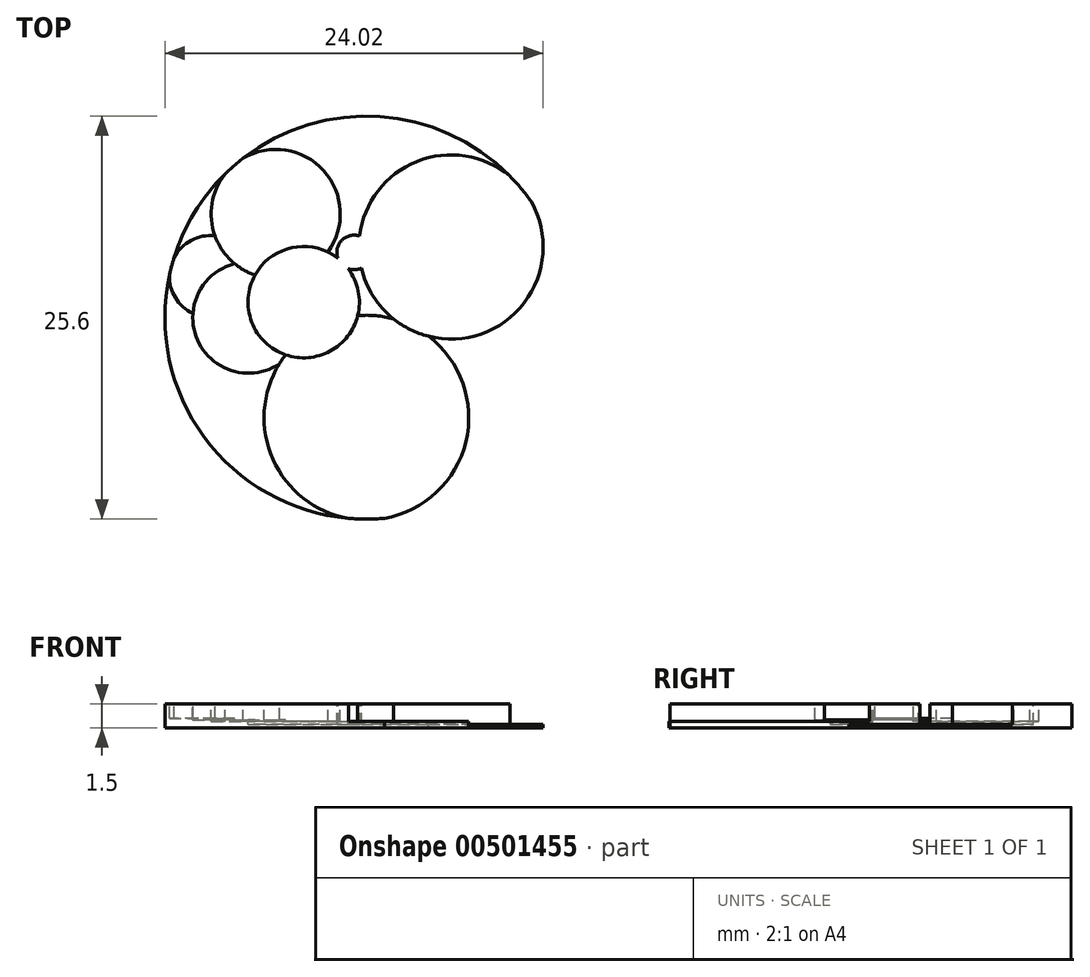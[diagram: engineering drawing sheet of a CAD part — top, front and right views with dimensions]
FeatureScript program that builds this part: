
annotation { "Feature Type Name" : "Feature", "Feature Type Description" : "" }
export const myFeature = defineFeature(function(context is Context, id is Id, definition is map)
    precondition{}
    {
        {
            var Q0;
            Q0=qCreatedBy(makeId("Top.planeOp"),FACE);
            var sketch = newSketch(context, id + "F0", { "sketchPlane" : qUnion([Q0])});
            skCircle(sketch, "E0", {"center": v(0, 0) * mm, "radius": 12.8 * mm});
            skCircle(sketch, "E1", {"center": v(5.37, 4.5) * mm, "radius": 5.65 * mm, "construction": true});
            skCircle(sketch, "E2", {"center": v(-0.78, 4.14) * mm, "radius": 4.05 * mm, "construction": true});
            skCircle(sketch, "E3", {"center": v(-0.78, 4.14) * mm, "radius": 0.9 * mm, "construction": true});
            skCircle(sketch, "E4", {"center": v(-3.98, 0.99) * mm, "radius": 3.34 * mm, "construction": true});
            skCircle(sketch, "E5", {"center": v(-3.98, 0.99) * mm, "radius": 0.63 * mm, "construction": true});
            skCircle(sketch, "E6", {"center": v(-7.5, 0) * mm, "radius": 3.33 * mm, "construction": true});
            skCircle(sketch, "E7", {"center": v(-7.5, 0) * mm, "radius": 0.47 * mm, "construction": true});
            skLineSegment(sketch, "E8", {"start": v(0, 12.8) * mm, "end": v(0, 5.1) * mm, "construction": true});
            skCircle(sketch, "E9", {"center": v(5.37, 4.5) * mm, "radius": 5.15 * mm, "construction": true});
            skCircle(sketch, "E10", {"center": v(0, -6.35) * mm, "radius": 6.3 * mm, "construction": true});
            skCircle(sketch, "E11", {"center": v(-9.91, 2.61) * mm, "radius": 0.38 * mm, "construction": true});
            skCircle(sketch, "E12", {"center": v(-9.91, 2.61) * mm, "radius": 2.4 * mm, "construction": true});
            skCircle(sketch, "E13", {"center": v(-5.76, 6.59) * mm, "radius": 3.85 * mm, "construction": true});
            skLineSegment(sketch, "E14", {"start": v(12.8, 0) * mm, "end": v(5.1, 0) * mm, "construction": true});
            skCircle(sketch, "E15", {"center": v(0, 5.4) * mm, "radius": 0.3 * mm, "construction": true});
            skCircle(sketch, "E16", {"center": v(5.37, 4.5) * mm, "radius": 6.16 * mm, "construction": true});
            skCircle(sketch, "E17", {"center": v(-0.78, 4.14) * mm, "radius": 4.5 * mm, "construction": true});
            skCircle(sketch, "E18", {"center": v(-3.98, 0.99) * mm, "radius": 3.65 * mm, "construction": true});
            skCircle(sketch, "E19", {"center": v(-7.5, 0) * mm, "radius": 3.56 * mm, "construction": true});
            skLineSegment(sketch, "E20", {"start": v(-9.91, 2.61) * mm, "end": v(-5.76, 6.59) * mm, "construction": true});
            skCircle(sketch, "E21", {"center": v(0, 6.2) * mm, "radius": 1.26 * mm, "construction": true});
            skCircle(sketch, "E22", {"center": v(0, 0) * mm, "radius": 1.16 * mm, "construction": true});
            skCircle(sketch, "E23", {"center": v(-0.78, 4.14) * mm, "radius": 1.16 * mm, "construction": true});
            skCircle(sketch, "E24", {"center": v(0, 6.2) * mm, "radius": 2.2 * mm, "construction": true});
            skCircle(sketch, "E25", {"center": v(0, 0) * mm, "radius": 2.81 * mm, "construction": true});
            skCircle(sketch, "E26", {"center": v(-5.76, 6.59) * mm, "radius": 2 * mm, "construction": true});
            skArc(sketch, "E27", {"start": v(1.14, -12.75) * mm, "mid": v(0, 0.15) * mm, "end": v(-1.14, -12.75) * mm});
            skCircle(sketch, "E28", {"center": v(-7.5, 0) * mm, "radius": 3.53 * mm});
            skArc(sketch, "E29", {"start": v(-12.5, 2.71) * mm, "mid": v(-7.4, 1.95) * mm, "end": v(-12.22, 3.8) * mm});
            skArc(sketch, "E30", {"start": v(9.1, 9) * mm, "mid": v(0.89, 0.74) * mm, "end": v(10.47, 7.36) * mm});
            skCircle(sketch, "E31", {"center": v(-3.98, 0.99) * mm, "radius": 3.54 * mm});
            skCircle(sketch, "E32", {"center": v(-0.78, 4.14) * mm, "radius": 1.1 * mm});
            skCircle(sketch, "E33", {"center": v(-5.76, 6.59) * mm, "radius": 4.1 * mm});
            skArc(sketch, "E34", {"start": v(-1.14, -12.75) * mm, "mid": v(0, -12.85) * mm, "end": v(1.14, -12.75) * mm});
            skArc(sketch, "E35", {"start": v(10.47, 7.36) * mm, "mid": v(9.86, 8.24) * mm, "end": v(9.1, 9) * mm});
            skArc(sketch, "E36", {"start": v(-12.22, 3.8) * mm, "mid": v(-12.43, 3.28) * mm, "end": v(-12.5, 2.71) * mm});
            skSolve(sketch);
        }
        {
            var Q0;
            {var subQ0=sQuery(id+"F0.wireOp",EDGE,"E31");var subQ1=sQuery(id+"F0.wireOp",EDGE,"E28");var subQ2=makeQuery(id+"F0.imprint","INTERSECT",VERTEX,{"disambiguationData":[OD(0.0)],"derivedFrom":[subQ1,subQ0]});Q0=makeQuery(id+"F0.imprint","IMPRINT",FACE,{"disambiguationData":[TD([[makeQuery(id+"F0.imprint","IMPRINT",EDGE,{"disambiguationData":[TD([[subQ2,1.0]])],"derivedFrom":subQ1}),1.0]])]});}
            var Q1;
            {var subQ0=sQuery(id+"F0.wireOp",EDGE,"E29");var subQ1=sQuery(id+"F0.wireOp",EDGE,"E0");var subQ2=makeQuery(id+"F0.imprint","INTERSECT",VERTEX,{"disambiguationData":[OD(1.0)],"derivedFrom":[subQ1,subQ0]});Q1=makeQuery(id+"F0.imprint","IMPRINT",FACE,{"disambiguationData":[TD([[makeQuery(id+"F0.imprint","IMPRINT",EDGE,{"disambiguationData":[TD([[subQ2,1.0]])],"derivedFrom":subQ1}),1.0]])]});}
            var Q2;
            {var subQ0=sQuery(id+"F0.wireOp",EDGE,"E28");var subQ1=sQuery(id+"F0.wireOp",EDGE,"E27");var subQ2=makeQuery(id+"F0.imprint","INTERSECT",VERTEX,{"disambiguationData":[OD(0.0)],"derivedFrom":[subQ1,subQ0]});Q2=makeQuery(id+"F0.imprint","IMPRINT",FACE,{"disambiguationData":[TD([[makeQuery(id+"F0.imprint","IMPRINT",EDGE,{"disambiguationData":[TD([[subQ2,-1.0]])],"derivedFrom":subQ1}),1.0]])]});}
            var Q3;
            {var subQ0=sQuery(id+"F0.wireOp",EDGE,"E31");var subQ1=sQuery(id+"F0.wireOp",EDGE,"E27");var subQ2=makeQuery(id+"F0.imprint","INTERSECT",VERTEX,{"disambiguationData":[OD(1.0)],"derivedFrom":[subQ1,subQ0]});Q3=makeQuery(id+"F0.imprint","IMPRINT",FACE,{"disambiguationData":[TD([[makeQuery(id+"F0.imprint","IMPRINT",EDGE,{"disambiguationData":[TD([[subQ2,-1.0]])],"derivedFrom":subQ1}),-1.0]])]});}
            var Q4;
            {var subQ0=sQuery(id+"F0.wireOp",EDGE,"E33");var subQ1=sQuery(id+"F0.wireOp",EDGE,"E28");var subQ2=makeQuery(id+"F0.imprint","INTERSECT",VERTEX,{"disambiguationData":[OD(1.0)],"derivedFrom":[subQ1,subQ0]});Q4=makeQuery(id+"F0.imprint","IMPRINT",FACE,{"disambiguationData":[TD([[makeQuery(id+"F0.imprint","IMPRINT",EDGE,{"disambiguationData":[TD([[subQ2,-1.0]])],"derivedFrom":subQ1}),1.0]])]});}
            var Q5;
            {var subQ0=sQuery(id+"F0.wireOp",EDGE,"E29");var subQ1=sQuery(id+"F0.wireOp",EDGE,"E0");var subQ5=makeQuery(id+"F0.imprint","INTERSECT",VERTEX,{"disambiguationData":[OD(0.0)],"derivedFrom":[subQ1,subQ0]});Q5=makeQuery(id+"F0.imprint","IMPRINT",FACE,{"disambiguationData":[TD([[makeQuery(id+"F0.imprint","IMPRINT",EDGE,{"disambiguationData":[TD([[subQ5,1.0]])],"derivedFrom":subQ1}),1.0]])]});}
            var Q6;
            {var subQ0=sQuery(id+"F0.wireOp",EDGE,"E32");var subQ1=sQuery(id+"F0.wireOp",EDGE,"E30");var subQ2=makeQuery(id+"F0.imprint","INTERSECT",VERTEX,{"disambiguationData":[OD(0.0)],"derivedFrom":[subQ1,subQ0]});Q6=makeQuery(id+"F0.imprint","IMPRINT",FACE,{"disambiguationData":[TD([[makeQuery(id+"F0.imprint","IMPRINT",EDGE,{"disambiguationData":[TD([[subQ2,-1.0]])],"derivedFrom":subQ1}),1.0]])]});}
            var Q7;
            {var subQ0=sQuery(id+"F0.wireOp",EDGE,"E29");var subQ1=sQuery(id+"F0.wireOp",EDGE,"E28");var subQ2=makeQuery(id+"F0.imprint","INTERSECT",VERTEX,{"disambiguationData":[OD(0.0)],"derivedFrom":[subQ1,subQ0]});Q7=makeQuery(id+"F0.imprint","IMPRINT",FACE,{"disambiguationData":[TD([[makeQuery(id+"F0.imprint","IMPRINT",EDGE,{"disambiguationData":[TD([[subQ2,-1.0]])],"derivedFrom":subQ1}),1.0]])]});}
            var Q8;
            {var subQ0=sQuery(id+"F0.wireOp",EDGE,"E29");var subQ1=sQuery(id+"F0.wireOp",EDGE,"E28");var subQ2=makeQuery(id+"F0.imprint","INTERSECT",VERTEX,{"disambiguationData":[OD(0.0)],"derivedFrom":[subQ1,subQ0]});Q8=makeQuery(id+"F0.imprint","IMPRINT",FACE,{"disambiguationData":[TD([[makeQuery(id+"F0.imprint","IMPRINT",EDGE,{"disambiguationData":[TD([[subQ2,-1.0]])],"derivedFrom":subQ1}),-1.0]])]});}
            var Q9;
            {var subQ4=sQuery(id+"F0.wireOp",EDGE,"E31");var subQ5=sQuery(id+"F0.wireOp",EDGE,"E28");var subQ6=makeQuery(id+"F0.imprint","INTERSECT",VERTEX,{"disambiguationData":[OD(0.0)],"derivedFrom":[subQ5,subQ4]});Q9=makeQuery(id+"F0.imprint","IMPRINT",FACE,{"disambiguationData":[TD([[makeQuery(id+"F0.imprint","IMPRINT",EDGE,{"disambiguationData":[TD([[subQ6,-1.0]])],"derivedFrom":subQ5}),-1.0]])]});}
            var Q10;
            {var subQ0=sQuery(id+"F0.wireOp",EDGE,"E31");var subQ1=sQuery(id+"F0.wireOp",EDGE,"E28");var subQ2=makeQuery(id+"F0.imprint","INTERSECT",VERTEX,{"disambiguationData":[OD(0.0)],"derivedFrom":[subQ1,subQ0]});Q10=makeQuery(id+"F0.imprint","IMPRINT",FACE,{"disambiguationData":[TD([[makeQuery(id+"F0.imprint","IMPRINT",EDGE,{"disambiguationData":[TD([[subQ2,-1.0]])],"derivedFrom":subQ1}),1.0]])]});}
            var Q11;
            {var subQ0=sQuery(id+"F0.wireOp",EDGE,"E31");var subQ1=sQuery(id+"F0.wireOp",EDGE,"E27");var subQ2=makeQuery(id+"F0.imprint","INTERSECT",VERTEX,{"disambiguationData":[OD(1.0)],"derivedFrom":[subQ1,subQ0]});Q11=makeQuery(id+"F0.imprint","IMPRINT",FACE,{"disambiguationData":[TD([[makeQuery(id+"F0.imprint","IMPRINT",EDGE,{"disambiguationData":[TD([[subQ2,-1.0]])],"derivedFrom":subQ1}),1.0]])]});}
            var Q12;
            {var subQ0=sQuery(id+"F0.wireOp",EDGE,"E31");var subQ1=sQuery(id+"F0.wireOp",EDGE,"E27");var subQ2=makeQuery(id+"F0.imprint","INTERSECT",VERTEX,{"disambiguationData":[OD(0.0)],"derivedFrom":[subQ1,subQ0]});Q12=makeQuery(id+"F0.imprint","IMPRINT",FACE,{"disambiguationData":[TD([[makeQuery(id+"F0.imprint","IMPRINT",EDGE,{"disambiguationData":[TD([[subQ2,-1.0]])],"derivedFrom":subQ1}),1.0]])]});}
            var Q13;
            {var subQ0=sQuery(id+"F0.wireOp",EDGE,"E31");var subQ1=sQuery(id+"F0.wireOp",EDGE,"E27");var subQ2=makeQuery(id+"F0.imprint","INTERSECT",VERTEX,{"disambiguationData":[OD(0.0)],"derivedFrom":[subQ1,subQ0]});Q13=makeQuery(id+"F0.imprint","IMPRINT",FACE,{"disambiguationData":[TD([[makeQuery(id+"F0.imprint","IMPRINT",EDGE,{"disambiguationData":[TD([[subQ2,-1.0]])],"derivedFrom":subQ1}),-1.0]])]});}
            var Q14;
            {var subQ0=sQuery(id+"F0.wireOp",EDGE,"E30");var subQ1=sQuery(id+"F0.wireOp",EDGE,"E27");var subQ2=makeQuery(id+"F0.imprint","INTERSECT",VERTEX,{"disambiguationData":[OD(0.0)],"derivedFrom":[subQ1,subQ0]});Q14=makeQuery(id+"F0.imprint","IMPRINT",FACE,{"disambiguationData":[TD([[makeQuery(id+"F0.imprint","IMPRINT",EDGE,{"disambiguationData":[TD([[subQ2,-1.0]])],"derivedFrom":subQ1}),1.0]])]});}
            var Q15;
            {var subQ0=sQuery(id+"F0.wireOp",EDGE,"E30");var subQ1=sQuery(id+"F0.wireOp",EDGE,"E27");var subQ2=makeQuery(id+"F0.imprint","INTERSECT",VERTEX,{"disambiguationData":[OD(1.0)],"derivedFrom":[subQ1,subQ0]});Q15=makeQuery(id+"F0.imprint","IMPRINT",FACE,{"disambiguationData":[TD([[makeQuery(id+"F0.imprint","IMPRINT",EDGE,{"disambiguationData":[TD([[subQ2,-1.0]])],"derivedFrom":subQ1}),-1.0]])]});}
            var Q16;
            {var subQ1=sQuery(id+"F0.wireOp",EDGE,"E30");var subQ7=sQuery(id+"F0.wireOp",EDGE,"E0");var subQ8=makeQuery(id+"F0.imprint","INTERSECT",VERTEX,{"disambiguationData":[OD(0.0)],"derivedFrom":[subQ7,subQ1]});Q16=makeQuery(id+"F0.imprint","IMPRINT",FACE,{"disambiguationData":[TD([[makeQuery(id+"F0.imprint","IMPRINT",EDGE,{"disambiguationData":[TD([[subQ8,-1.0]])],"derivedFrom":subQ7}),1.0]])]});}
            var Q17;
            {var subQ0=sQuery(id+"F0.wireOp",EDGE,"E31");var subQ1=sQuery(id+"F0.wireOp",EDGE,"E28");var subQ2=makeQuery(id+"F0.imprint","INTERSECT",VERTEX,{"disambiguationData":[OD(0.0)],"derivedFrom":[subQ1,subQ0]});Q17=makeQuery(id+"F0.imprint","IMPRINT",FACE,{"disambiguationData":[TD([[makeQuery(id+"F0.imprint","IMPRINT",EDGE,{"disambiguationData":[TD([[subQ2,1.0]])],"derivedFrom":subQ1}),-1.0]])]});}
            var Q18;
            {var subQ0=sQuery(id+"F0.wireOp",EDGE,"E28");var subQ1=sQuery(id+"F0.wireOp",EDGE,"E27");var subQ2=makeQuery(id+"F0.imprint","INTERSECT",VERTEX,{"disambiguationData":[OD(0.0)],"derivedFrom":[subQ1,subQ0]});Q18=makeQuery(id+"F0.imprint","IMPRINT",FACE,{"disambiguationData":[TD([[makeQuery(id+"F0.imprint","IMPRINT",EDGE,{"disambiguationData":[TD([[subQ2,-1.0]])],"derivedFrom":subQ1}),-1.0]])]});}
            var Q19;
            {var subQ0=sQuery(id+"F0.wireOp",EDGE,"E30");var subQ5=sQuery(id+"F0.wireOp",EDGE,"E0");var subQ6=makeQuery(id+"F0.imprint","INTERSECT",VERTEX,{"disambiguationData":[OD(0.0)],"derivedFrom":[subQ5,subQ0]});Q19=makeQuery(id+"F0.imprint","IMPRINT",FACE,{"disambiguationData":[TD([[makeQuery(id+"F0.imprint","IMPRINT",EDGE,{"disambiguationData":[TD([[subQ6,1.0]])],"derivedFrom":subQ5}),1.0]])]});}
            var Q20;
            {var subQ0=sQuery(id+"F0.wireOp",EDGE,"E32");var subQ1=sQuery(id+"F0.wireOp",EDGE,"E30");var subQ2=makeQuery(id+"F0.imprint","INTERSECT",VERTEX,{"disambiguationData":[OD(0.0)],"derivedFrom":[subQ1,subQ0]});Q20=makeQuery(id+"F0.imprint","IMPRINT",FACE,{"disambiguationData":[TD([[makeQuery(id+"F0.imprint","IMPRINT",EDGE,{"disambiguationData":[TD([[subQ2,-1.0]])],"derivedFrom":subQ1}),-1.0]])]});}
            var Q21;
            {var subQ0=sQuery(id+"F0.wireOp",EDGE,"E32");var subQ1=sQuery(id+"F0.wireOp",EDGE,"E31");var subQ2=makeQuery(id+"F0.imprint","INTERSECT",VERTEX,{"disambiguationData":[OD(0.0)],"derivedFrom":[subQ1,subQ0]});Q21=makeQuery(id+"F0.imprint","IMPRINT",FACE,{"disambiguationData":[TD([[makeQuery(id+"F0.imprint","IMPRINT",EDGE,{"disambiguationData":[TD([[subQ2,1.0]])],"derivedFrom":subQ1}),1.0]])]});}
            var Q22;
            {var subQ0=sQuery(id+"F0.wireOp",EDGE,"E27");var subQ1=sQuery(id+"F0.wireOp",EDGE,"E0");var subQ9=makeQuery(id+"F0.imprint","INTERSECT",VERTEX,{"disambiguationData":[OD(0.0)],"derivedFrom":[subQ1,subQ0]});Q22=makeQuery(id+"F0.imprint","IMPRINT",FACE,{"disambiguationData":[TD([[makeQuery(id+"F0.imprint","IMPRINT",EDGE,{"disambiguationData":[TD([[subQ9,1.0]])],"derivedFrom":subQ1}),1.0]])]});}
            var Q23;
            {var subQ0=sQuery(id+"F0.wireOp",EDGE,"E27");var subQ1=sQuery(id+"F0.wireOp",EDGE,"E0");var subQ2=makeQuery(id+"F0.imprint","INTERSECT",VERTEX,{"disambiguationData":[OD(1.0)],"derivedFrom":[subQ1,subQ0]});Q23=makeQuery(id+"F0.imprint","IMPRINT",FACE,{"disambiguationData":[TD([[makeQuery(id+"F0.imprint","IMPRINT",EDGE,{"disambiguationData":[TD([[subQ2,1.0]])],"derivedFrom":subQ1}),1.0]])]});}
            var Q24;
            {var subQ0=sQuery(id+"F0.wireOp",EDGE,"E27");var subQ1=sQuery(id+"F0.wireOp",EDGE,"E0");var subQ2=makeQuery(id+"F0.imprint","INTERSECT",VERTEX,{"disambiguationData":[OD(0.0)],"derivedFrom":[subQ1,subQ0]});Q24=makeQuery(id+"F0.imprint","IMPRINT",FACE,{"disambiguationData":[TD([[makeQuery(id+"F0.imprint","IMPRINT",EDGE,{"disambiguationData":[TD([[subQ2,-1.0]])],"derivedFrom":subQ1}),1.0]])]});}
            extrude(context, id + "F1", {"entities" : qUnion([Q0, Q1, Q2, Q3, Q4, Q5, Q6, Q7, Q8, Q9, Q10, Q11, Q12, Q13, Q14, Q15, Q16, Q17, Q18, Q19, Q20, Q21, Q22, Q23, Q24]), "oppositeDirection" : true, "depth" : 1.5 * mm, "offsetDistance" : 25 * mm});
        }
        {
            var Q0;
            {var subQ0=sQuery(id+"F0.wireOp",EDGE,"E34");Q0=makeQuery(id+"F0.imprint","IMPRINT",FACE,{"disambiguationData":[TD([[makeQuery(id+"F0.imprint","IMPRINT",EDGE,{"derivedFrom":subQ0}),1.0]])]});}
            var Q1;
            {var subQ1=sQuery(id+"F0.wireOp",EDGE,"E27");var subQ6=sQuery(id+"F0.wireOp",EDGE,"E30");var subQ7=makeQuery(id+"F0.imprint","INTERSECT",VERTEX,{"disambiguationData":[OD(1.0)],"derivedFrom":[subQ1,subQ6]});Q1=makeQuery(id+"F0.imprint","IMPRINT",FACE,{"disambiguationData":[TD([[makeQuery(id+"F0.imprint","IMPRINT",EDGE,{"disambiguationData":[TD([[subQ7,-1.0]])],"derivedFrom":subQ1}),1.0]])]});}
            var Q2;
            {var subQ0=sQuery(id+"F0.wireOp",EDGE,"E30");var subQ1=sQuery(id+"F0.wireOp",EDGE,"E27");var subQ2=makeQuery(id+"F0.imprint","INTERSECT",VERTEX,{"disambiguationData":[OD(0.0)],"derivedFrom":[subQ1,subQ0]});Q2=makeQuery(id+"F0.imprint","IMPRINT",FACE,{"disambiguationData":[TD([[makeQuery(id+"F0.imprint","IMPRINT",EDGE,{"disambiguationData":[TD([[subQ2,-1.0]])],"derivedFrom":subQ1}),1.0]])]});}
            var Q3;
            {var subQ0=sQuery(id+"F0.wireOp",EDGE,"E31");var subQ1=sQuery(id+"F0.wireOp",EDGE,"E27");var subQ2=makeQuery(id+"F0.imprint","INTERSECT",VERTEX,{"disambiguationData":[OD(0.0)],"derivedFrom":[subQ1,subQ0]});Q3=makeQuery(id+"F0.imprint","IMPRINT",FACE,{"disambiguationData":[TD([[makeQuery(id+"F0.imprint","IMPRINT",EDGE,{"disambiguationData":[TD([[subQ2,-1.0]])],"derivedFrom":subQ1}),1.0]])]});}
            var Q4;
            {var subQ0=sQuery(id+"F0.wireOp",EDGE,"E28");var subQ1=sQuery(id+"F0.wireOp",EDGE,"E27");var subQ2=makeQuery(id+"F0.imprint","INTERSECT",VERTEX,{"disambiguationData":[OD(0.0)],"derivedFrom":[subQ1,subQ0]});Q4=makeQuery(id+"F0.imprint","IMPRINT",FACE,{"disambiguationData":[TD([[makeQuery(id+"F0.imprint","IMPRINT",EDGE,{"disambiguationData":[TD([[subQ2,-1.0]])],"derivedFrom":subQ1}),1.0]])]});}
            var Q5;
            {var subQ0=sQuery(id+"F0.wireOp",EDGE,"E31");var subQ1=sQuery(id+"F0.wireOp",EDGE,"E27");var subQ2=makeQuery(id+"F0.imprint","INTERSECT",VERTEX,{"disambiguationData":[OD(1.0)],"derivedFrom":[subQ1,subQ0]});Q5=makeQuery(id+"F0.imprint","IMPRINT",FACE,{"disambiguationData":[TD([[makeQuery(id+"F0.imprint","IMPRINT",EDGE,{"disambiguationData":[TD([[subQ2,-1.0]])],"derivedFrom":subQ1}),1.0]])]});}
            extrude(context, id + "F2", {"entities" : qUnion([Q0, Q1, Q2, Q3, Q4, Q5]), "operationType" : NewBodyOperationType.REMOVE, "oppositeDirection" : true, "depth" : 1.1 * mm, "offsetDistance" : 25 * mm});
        }
        {
            var Q0;
            {var subQ0=sQuery(id+"F0.wireOp",EDGE,"E28");var subQ1=sQuery(id+"F0.wireOp",EDGE,"E27");var subQ2=makeQuery(id+"F0.imprint","INTERSECT",VERTEX,{"disambiguationData":[OD(0.0)],"derivedFrom":[subQ1,subQ0]});Q0=makeQuery(id+"F0.imprint","IMPRINT",FACE,{"disambiguationData":[TD([[makeQuery(id+"F0.imprint","IMPRINT",EDGE,{"disambiguationData":[TD([[subQ2,-1.0]])],"derivedFrom":subQ1}),-1.0]])]});}
            var Q1;
            {var subQ0=sQuery(id+"F0.wireOp",EDGE,"E31");var subQ1=sQuery(id+"F0.wireOp",EDGE,"E27");var subQ2=makeQuery(id+"F0.imprint","INTERSECT",VERTEX,{"disambiguationData":[OD(0.0)],"derivedFrom":[subQ1,subQ0]});Q1=makeQuery(id+"F0.imprint","IMPRINT",FACE,{"disambiguationData":[TD([[makeQuery(id+"F0.imprint","IMPRINT",EDGE,{"disambiguationData":[TD([[subQ2,-1.0]])],"derivedFrom":subQ1}),-1.0]])]});}
            var Q2;
            {var subQ0=sQuery(id+"F0.wireOp",EDGE,"E31");var subQ1=sQuery(id+"F0.wireOp",EDGE,"E28");var subQ2=makeQuery(id+"F0.imprint","INTERSECT",VERTEX,{"disambiguationData":[OD(0.0)],"derivedFrom":[subQ1,subQ0]});Q2=makeQuery(id+"F0.imprint","IMPRINT",FACE,{"disambiguationData":[TD([[makeQuery(id+"F0.imprint","IMPRINT",EDGE,{"disambiguationData":[TD([[subQ2,1.0]])],"derivedFrom":subQ1}),-1.0]])]});}
            var Q3;
            {var subQ0=sQuery(id+"F0.wireOp",EDGE,"E31");var subQ1=sQuery(id+"F0.wireOp",EDGE,"E28");var subQ2=makeQuery(id+"F0.imprint","INTERSECT",VERTEX,{"disambiguationData":[OD(0.0)],"derivedFrom":[subQ1,subQ0]});Q3=makeQuery(id+"F0.imprint","IMPRINT",FACE,{"disambiguationData":[TD([[makeQuery(id+"F0.imprint","IMPRINT",EDGE,{"disambiguationData":[TD([[subQ2,1.0]])],"derivedFrom":subQ1}),1.0]])]});}
            var Q4;
            {var subQ0=sQuery(id+"F0.wireOp",EDGE,"E31");var subQ1=sQuery(id+"F0.wireOp",EDGE,"E27");var subQ2=makeQuery(id+"F0.imprint","INTERSECT",VERTEX,{"disambiguationData":[OD(0.0)],"derivedFrom":[subQ1,subQ0]});Q4=makeQuery(id+"F0.imprint","IMPRINT",FACE,{"disambiguationData":[TD([[makeQuery(id+"F0.imprint","IMPRINT",EDGE,{"disambiguationData":[TD([[subQ2,-1.0]])],"derivedFrom":subQ1}),1.0]])]});}
            var Q5;
            {var subQ0=sQuery(id+"F0.wireOp",EDGE,"E28");var subQ1=sQuery(id+"F0.wireOp",EDGE,"E27");var subQ2=makeQuery(id+"F0.imprint","INTERSECT",VERTEX,{"disambiguationData":[OD(0.0)],"derivedFrom":[subQ1,subQ0]});Q5=makeQuery(id+"F0.imprint","IMPRINT",FACE,{"disambiguationData":[TD([[makeQuery(id+"F0.imprint","IMPRINT",EDGE,{"disambiguationData":[TD([[subQ2,-1.0]])],"derivedFrom":subQ1}),1.0]])]});}
            var Q6;
            {var subQ0=sQuery(id+"F0.wireOp",EDGE,"E32");var subQ1=sQuery(id+"F0.wireOp",EDGE,"E31");var subQ2=makeQuery(id+"F0.imprint","INTERSECT",VERTEX,{"disambiguationData":[OD(0.0)],"derivedFrom":[subQ1,subQ0]});Q6=makeQuery(id+"F0.imprint","IMPRINT",FACE,{"disambiguationData":[TD([[makeQuery(id+"F0.imprint","IMPRINT",EDGE,{"disambiguationData":[TD([[subQ2,1.0]])],"derivedFrom":subQ1}),1.0]])]});}
            extrude(context, id + "F3", {"entities" : qUnion([Q0, Q1, Q2, Q3, Q4, Q5, Q6]), "operationType" : NewBodyOperationType.REMOVE, "oppositeDirection" : true, "depth" : 1.3 * mm, "offsetDistance" : 25 * mm});
        }
        {
            var Q0;
            {var subQ0=sQuery(id+"F0.wireOp",EDGE,"E31");var subQ1=sQuery(id+"F0.wireOp",EDGE,"E27");var subQ2=makeQuery(id+"F0.imprint","INTERSECT",VERTEX,{"disambiguationData":[OD(1.0)],"derivedFrom":[subQ1,subQ0]});Q0=makeQuery(id+"F0.imprint","IMPRINT",FACE,{"disambiguationData":[TD([[makeQuery(id+"F0.imprint","IMPRINT",EDGE,{"disambiguationData":[TD([[subQ2,-1.0]])],"derivedFrom":subQ1}),-1.0]])]});}
            var Q1;
            {var subQ0=sQuery(id+"F0.wireOp",EDGE,"E33");var subQ1=sQuery(id+"F0.wireOp",EDGE,"E28");var subQ2=makeQuery(id+"F0.imprint","INTERSECT",VERTEX,{"disambiguationData":[OD(1.0)],"derivedFrom":[subQ1,subQ0]});Q1=makeQuery(id+"F0.imprint","IMPRINT",FACE,{"disambiguationData":[TD([[makeQuery(id+"F0.imprint","IMPRINT",EDGE,{"disambiguationData":[TD([[subQ2,-1.0]])],"derivedFrom":subQ1}),1.0]])]});}
            var Q2;
            {var subQ0=sQuery(id+"F0.wireOp",EDGE,"E29");var subQ1=sQuery(id+"F0.wireOp",EDGE,"E28");var subQ2=makeQuery(id+"F0.imprint","INTERSECT",VERTEX,{"disambiguationData":[OD(0.0)],"derivedFrom":[subQ1,subQ0]});Q2=makeQuery(id+"F0.imprint","IMPRINT",FACE,{"disambiguationData":[TD([[makeQuery(id+"F0.imprint","IMPRINT",EDGE,{"disambiguationData":[TD([[subQ2,-1.0]])],"derivedFrom":subQ1}),1.0]])]});}
            var Q3;
            {var subQ0=sQuery(id+"F0.wireOp",EDGE,"E31");var subQ1=sQuery(id+"F0.wireOp",EDGE,"E28");var subQ2=makeQuery(id+"F0.imprint","INTERSECT",VERTEX,{"disambiguationData":[OD(0.0)],"derivedFrom":[subQ1,subQ0]});Q3=makeQuery(id+"F0.imprint","IMPRINT",FACE,{"disambiguationData":[TD([[makeQuery(id+"F0.imprint","IMPRINT",EDGE,{"disambiguationData":[TD([[subQ2,-1.0]])],"derivedFrom":subQ1}),1.0]])]});}
            extrude(context, id + "F4", {"entities" : qUnion([Q0, Q1, Q2, Q3]), "operationType" : NewBodyOperationType.REMOVE, "oppositeDirection" : true, "depth" : 1 * mm, "offsetDistance" : 25 * mm});
        }
        {
            var Q0;
            {var subQ4=sQuery(id+"F0.wireOp",EDGE,"E33");var subQ7=sQuery(id+"F0.wireOp",EDGE,"E28");var subQ9=makeQuery(id+"F0.imprint","INTERSECT",VERTEX,{"disambiguationData":[OD(1.0)],"derivedFrom":[subQ7,subQ4]});Q0=makeQuery(id+"F0.imprint","IMPRINT",FACE,{"disambiguationData":[TD([[makeQuery(id+"F0.imprint","IMPRINT",EDGE,{"disambiguationData":[TD([[subQ9,-1.0]])],"derivedFrom":subQ7}),-1.0]])]});}
            var Q1;
            {var subQ0=sQuery(id+"F0.wireOp",EDGE,"E29");var subQ1=sQuery(id+"F0.wireOp",EDGE,"E28");var subQ2=makeQuery(id+"F0.imprint","INTERSECT",VERTEX,{"disambiguationData":[OD(0.0)],"derivedFrom":[subQ1,subQ0]});Q1=makeQuery(id+"F0.imprint","IMPRINT",FACE,{"disambiguationData":[TD([[makeQuery(id+"F0.imprint","IMPRINT",EDGE,{"disambiguationData":[TD([[subQ2,-1.0]])],"derivedFrom":subQ1}),-1.0]])]});}
            extrude(context, id + "F5", {"entities" : qUnion([Q0, Q1]), "operationType" : NewBodyOperationType.REMOVE, "oppositeDirection" : true, "depth" : 0.9 * mm, "offsetDistance" : 25 * mm});
        }
        {
            var Q0;
            {var subQ0=sQuery(id+"F0.wireOp",EDGE,"E30");var subQ1=sQuery(id+"F0.wireOp",EDGE,"E27");var subQ9=makeQuery(id+"F0.imprint","INTERSECT",VERTEX,{"disambiguationData":[OD(0.0)],"derivedFrom":[subQ1,subQ0]});Q0=makeQuery(id+"F0.imprint","IMPRINT",FACE,{"disambiguationData":[TD([[makeQuery(id+"F0.imprint","IMPRINT",EDGE,{"disambiguationData":[TD([[subQ9,-1.0]])],"derivedFrom":subQ1}),-1.0]])]});}
            var Q1;
            {var subQ0=sQuery(id+"F0.wireOp",EDGE,"E32");var subQ1=sQuery(id+"F0.wireOp",EDGE,"E30");var subQ2=makeQuery(id+"F0.imprint","INTERSECT",VERTEX,{"disambiguationData":[OD(0.0)],"derivedFrom":[subQ1,subQ0]});Q1=makeQuery(id+"F0.imprint","IMPRINT",FACE,{"disambiguationData":[TD([[makeQuery(id+"F0.imprint","IMPRINT",EDGE,{"disambiguationData":[TD([[subQ2,-1.0]])],"derivedFrom":subQ1}),1.0]])]});}
            var Q2;
            {var subQ0=sQuery(id+"F0.wireOp",EDGE,"E30");var subQ1=sQuery(id+"F0.wireOp",EDGE,"E27");var subQ2=makeQuery(id+"F0.imprint","INTERSECT",VERTEX,{"disambiguationData":[OD(0.0)],"derivedFrom":[subQ1,subQ0]});Q2=makeQuery(id+"F0.imprint","IMPRINT",FACE,{"disambiguationData":[TD([[makeQuery(id+"F0.imprint","IMPRINT",EDGE,{"disambiguationData":[TD([[subQ2,-1.0]])],"derivedFrom":subQ1}),1.0]])]});}
            var Q3;
            {var subQ0=sQuery(id+"F0.wireOp",EDGE,"E35");Q3=makeQuery(id+"F0.imprint","IMPRINT",FACE,{"disambiguationData":[TD([[makeQuery(id+"F0.imprint","IMPRINT",EDGE,{"derivedFrom":subQ0}),1.0]])]});}
            extrude(context, id + "F6", {"entities" : qUnion([Q0, Q1, Q2, Q3]), "operationType" : NewBodyOperationType.REMOVE, "oppositeDirection" : true, "depth" : 1.3 * mm, "offsetDistance" : 25 * mm});
        }
        {
            var Q0;
            {var subQ0=sQuery(id+"F0.wireOp",EDGE,"E32");var subQ1=sQuery(id+"F0.wireOp",EDGE,"E30");var subQ2=makeQuery(id+"F0.imprint","INTERSECT",VERTEX,{"disambiguationData":[OD(0.0)],"derivedFrom":[subQ1,subQ0]});Q0=makeQuery(id+"F0.imprint","IMPRINT",FACE,{"disambiguationData":[TD([[makeQuery(id+"F0.imprint","IMPRINT",EDGE,{"disambiguationData":[TD([[subQ2,-1.0]])],"derivedFrom":subQ1}),-1.0]])]});}
            var Q1;
            {var subQ0=sQuery(id+"F0.wireOp",EDGE,"E32");var subQ1=sQuery(id+"F0.wireOp",EDGE,"E30");var subQ2=makeQuery(id+"F0.imprint","INTERSECT",VERTEX,{"disambiguationData":[OD(0.0)],"derivedFrom":[subQ1,subQ0]});Q1=makeQuery(id+"F0.imprint","IMPRINT",FACE,{"disambiguationData":[TD([[makeQuery(id+"F0.imprint","IMPRINT",EDGE,{"disambiguationData":[TD([[subQ2,-1.0]])],"derivedFrom":subQ1}),1.0]])]});}
            var Q2;
            {var subQ0=sQuery(id+"F0.wireOp",EDGE,"E32");var subQ1=sQuery(id+"F0.wireOp",EDGE,"E31");var subQ2=makeQuery(id+"F0.imprint","INTERSECT",VERTEX,{"disambiguationData":[OD(0.0)],"derivedFrom":[subQ1,subQ0]});Q2=makeQuery(id+"F0.imprint","IMPRINT",FACE,{"disambiguationData":[TD([[makeQuery(id+"F0.imprint","IMPRINT",EDGE,{"disambiguationData":[TD([[subQ2,1.0]])],"derivedFrom":subQ1}),1.0]])]});}
            extrude(context, id + "F7", {"entities" : qUnion([Q0, Q1, Q2]), "operationType" : NewBodyOperationType.REMOVE, "oppositeDirection" : true, "depth" : 1.3 * mm, "offsetDistance" : 25 * mm});
        }
        {
            var Q0;
            {var subQ3=sQuery(id+"F0.wireOp",EDGE,"E33");var subQ5=sQuery(id+"F0.wireOp",EDGE,"E0");var subQ6=makeQuery(id+"F0.imprint","INTERSECT",VERTEX,{"disambiguationData":[OD(0.0)],"derivedFrom":[subQ5,subQ3]});Q0=makeQuery(id+"F0.imprint","IMPRINT",FACE,{"disambiguationData":[TD([[makeQuery(id+"F0.imprint","IMPRINT",EDGE,{"disambiguationData":[TD([[subQ6,-1.0]])],"derivedFrom":subQ5}),1.0]])]});}
            var Q1;
            {var subQ0=sQuery(id+"F0.wireOp",EDGE,"E29");var subQ1=sQuery(id+"F0.wireOp",EDGE,"E28");var subQ2=makeQuery(id+"F0.imprint","INTERSECT",VERTEX,{"disambiguationData":[OD(0.0)],"derivedFrom":[subQ1,subQ0]});Q1=makeQuery(id+"F0.imprint","IMPRINT",FACE,{"disambiguationData":[TD([[makeQuery(id+"F0.imprint","IMPRINT",EDGE,{"disambiguationData":[TD([[subQ2,-1.0]])],"derivedFrom":subQ1}),-1.0]])]});}
            var Q2;
            {var subQ0=sQuery(id+"F0.wireOp",EDGE,"E31");var subQ1=sQuery(id+"F0.wireOp",EDGE,"E28");var subQ2=makeQuery(id+"F0.imprint","INTERSECT",VERTEX,{"disambiguationData":[OD(0.0)],"derivedFrom":[subQ1,subQ0]});Q2=makeQuery(id+"F0.imprint","IMPRINT",FACE,{"disambiguationData":[TD([[makeQuery(id+"F0.imprint","IMPRINT",EDGE,{"disambiguationData":[TD([[subQ2,1.0]])],"derivedFrom":subQ1}),-1.0]])]});}
            var Q3;
            {var subQ0=sQuery(id+"F0.wireOp",EDGE,"E31");var subQ1=sQuery(id+"F0.wireOp",EDGE,"E28");var subQ2=makeQuery(id+"F0.imprint","INTERSECT",VERTEX,{"disambiguationData":[OD(0.0)],"derivedFrom":[subQ1,subQ0]});Q3=makeQuery(id+"F0.imprint","IMPRINT",FACE,{"disambiguationData":[TD([[makeQuery(id+"F0.imprint","IMPRINT",EDGE,{"disambiguationData":[TD([[subQ2,1.0]])],"derivedFrom":subQ1}),1.0]])]});}
            var Q4;
            {var subQ0=sQuery(id+"F0.wireOp",EDGE,"E29");var subQ1=sQuery(id+"F0.wireOp",EDGE,"E28");var subQ2=makeQuery(id+"F0.imprint","INTERSECT",VERTEX,{"disambiguationData":[OD(0.0)],"derivedFrom":[subQ1,subQ0]});Q4=makeQuery(id+"F0.imprint","IMPRINT",FACE,{"disambiguationData":[TD([[makeQuery(id+"F0.imprint","IMPRINT",EDGE,{"disambiguationData":[TD([[subQ2,-1.0]])],"derivedFrom":subQ1}),1.0]])]});}
            var Q5;
            {var subQ0=sQuery(id+"F0.wireOp",EDGE,"E31");var subQ1=sQuery(id+"F0.wireOp",EDGE,"E28");var subQ2=makeQuery(id+"F0.imprint","INTERSECT",VERTEX,{"disambiguationData":[OD(0.0)],"derivedFrom":[subQ1,subQ0]});Q5=makeQuery(id+"F0.imprint","IMPRINT",FACE,{"disambiguationData":[TD([[makeQuery(id+"F0.imprint","IMPRINT",EDGE,{"disambiguationData":[TD([[subQ2,-1.0]])],"derivedFrom":subQ1}),1.0]])]});}
            extrude(context, id + "F8", {"entities" : qUnion([Q0, Q1, Q2, Q3, Q4, Q5]), "operationType" : NewBodyOperationType.REMOVE, "oppositeDirection" : true, "depth" : 1.1 * mm, "offsetDistance" : 25 * mm});
        }
    });
